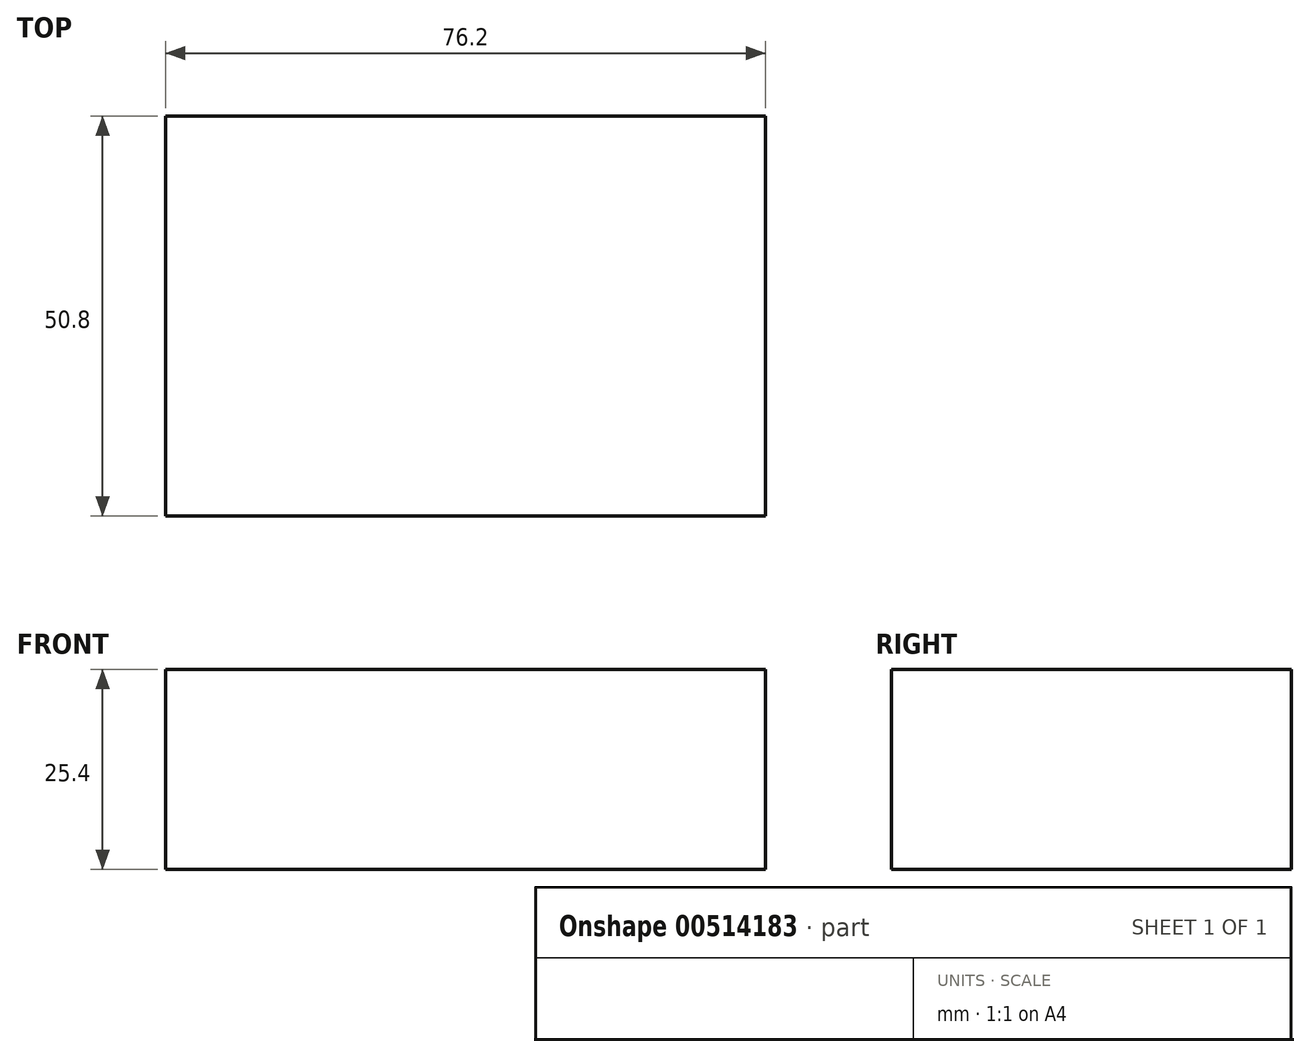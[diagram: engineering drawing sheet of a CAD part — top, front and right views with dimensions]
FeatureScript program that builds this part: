
annotation { "Feature Type Name" : "Feature", "Feature Type Description" : "" }
export const myFeature = defineFeature(function(context is Context, id is Id, definition is map)
    precondition{}
    {
        {
            var Q0;
            Q0=qCreatedBy(makeId("Front.planeOp"),FACE);
            var sketch = newSketch(context, id + "F0", { "sketchPlane" : qUnion([Q0])});
            skLineSegment(sketch, "E0.bottom", {"start": v(0, 0) * mm, "end": v(76.2, 0) * mm});
            skLineSegment(sketch, "E0.top", {"start": v(0, 25.4) * mm, "end": v(76.2, 25.4) * mm});
            skLineSegment(sketch, "E0.left", {"start": v(0, 0) * mm, "end": v(0, 25.4) * mm});
            skLineSegment(sketch, "E0.right", {"start": v(76.2, 0) * mm, "end": v(76.2, 25.4) * mm});
            skSolve(sketch);
        }
        {
            var Q0;
            Q0 = qSketchRegion(id + "F0", true);
            extrude(context, id + "F1", {"entities" : qUnion([Q0]), "depth" : 50.8 * mm});
        }
    });
